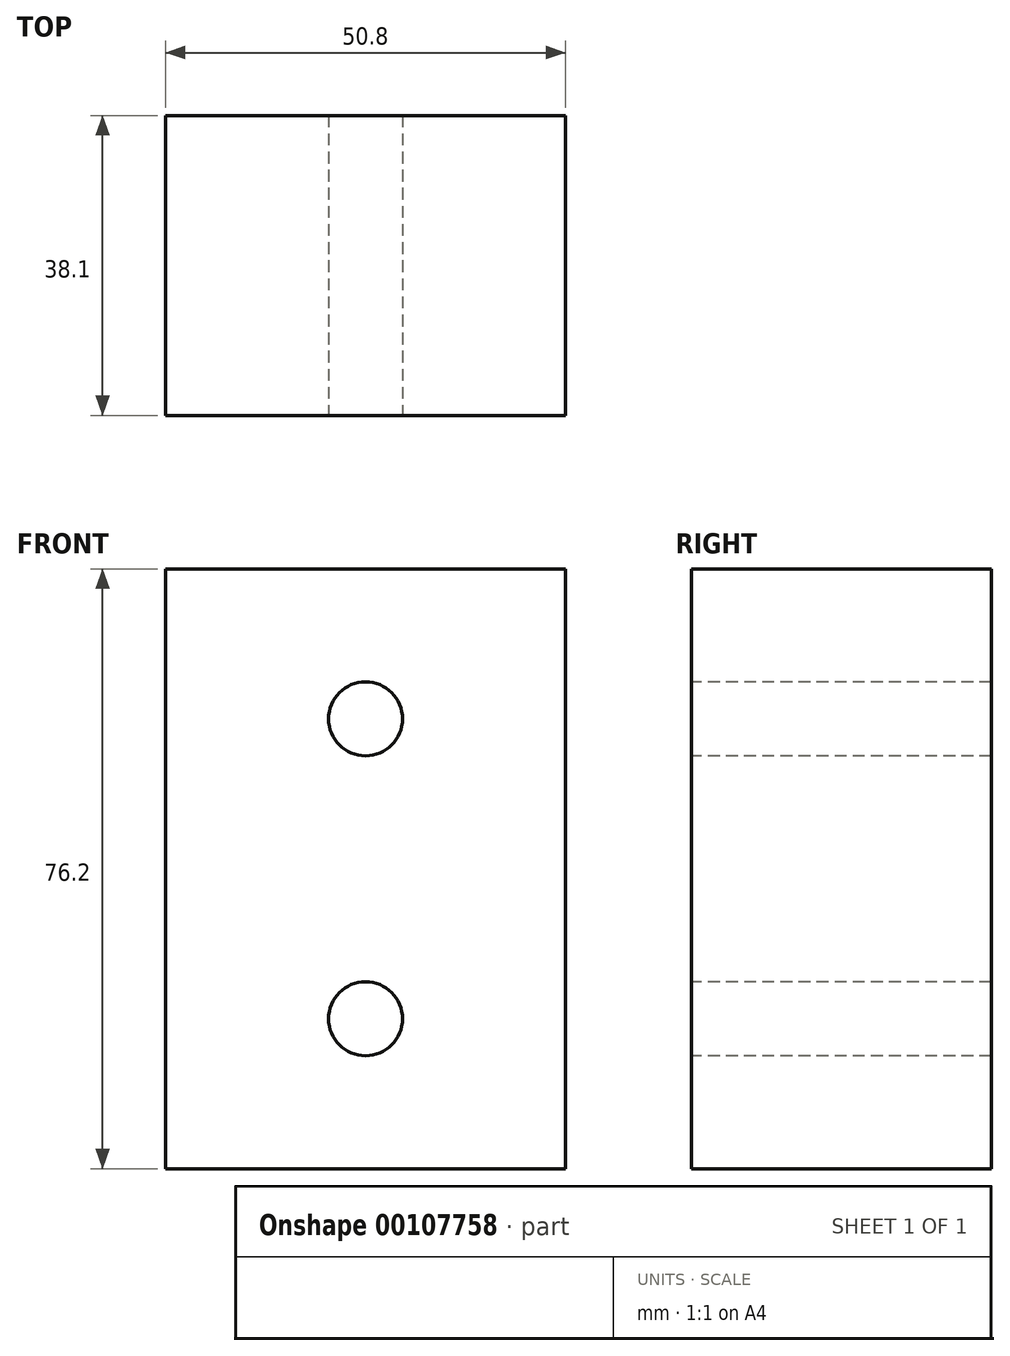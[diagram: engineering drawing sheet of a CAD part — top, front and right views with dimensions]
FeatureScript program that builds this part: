
annotation { "Feature Type Name" : "Feature", "Feature Type Description" : "" }
export const myFeature = defineFeature(function(context is Context, id is Id, definition is map)
    precondition{}
    {
        {
            var Q0;
            Q0=qCreatedBy(makeId("Front.planeOp"),FACE);
            var sketch = newSketch(context, id + "F0", { "sketchPlane" : qUnion([Q0])});
            skLineSegment(sketch, "E0.bottom", {"start": v(-25.4, 38.1) * mm, "end": v(25.4, 38.1) * mm});
            skLineSegment(sketch, "E0.top", {"start": v(-25.4, -38.1) * mm, "end": v(25.4, -38.1) * mm});
            skLineSegment(sketch, "E0.left", {"start": v(-25.4, 38.1) * mm, "end": v(-25.4, -38.1) * mm});
            skLineSegment(sketch, "E0.right", {"start": v(25.4, 38.1) * mm, "end": v(25.4, -38.1) * mm});
            skPoint(sketch, "E1.start.orphan", {"position": v(0, -38.1) * mm});
            skPoint(sketch, "E2.start.orphan", {"position": v(0, 38.1) * mm});
            skSolve(sketch);
        }
        {
            var Q0;
            Q0 = qSketchRegion(id + "F0", true);
            extrude(context, id + "F1", {"entities" : qUnion([Q0]), "depth" : 38.1 * mm});
        }
        {
            var Q0;
            Q0=makeQuery(id+"F1.opExtrude","CAP_FACE",FACE,{"disambiguationData":[OSD([sQuery(id+"F0.wireOp",EDGE,"E0.bottom"),sQuery(id+"F0.wireOp",EDGE,"E0.top"),sQuery(id+"F0.wireOp",EDGE,"E0.left"),sQuery(id+"F0.wireOp",EDGE,"E0.right")])],"isStart":false});
            var sketch = newSketch(context, id + "F2", { "sketchPlane" : qUnion([Q0])});
            skPoint(sketch, "E3.endSnap0", {"position": v(0, 38.1) * mm});
            skCircle(sketch, "E4", {"center": v(0, 19.05) * mm, "radius": 4.7 * mm});
            skCircle(sketch, "E5", {"center": v(0, -19.05) * mm, "radius": 4.7 * mm});
            skSolve(sketch);
        }
        {
            var Q0;
            Q0 = qSketchRegion(id + "F2", true);
            extrude(context, id + "F3", {"entities" : qUnion([Q0]), "operationType" : NewBodyOperationType.REMOVE, "endBound" : BoundingType.THROUGH_ALL, "oppositeDirection" : true, "depth" : 25.4 * mm});
        }
    });
